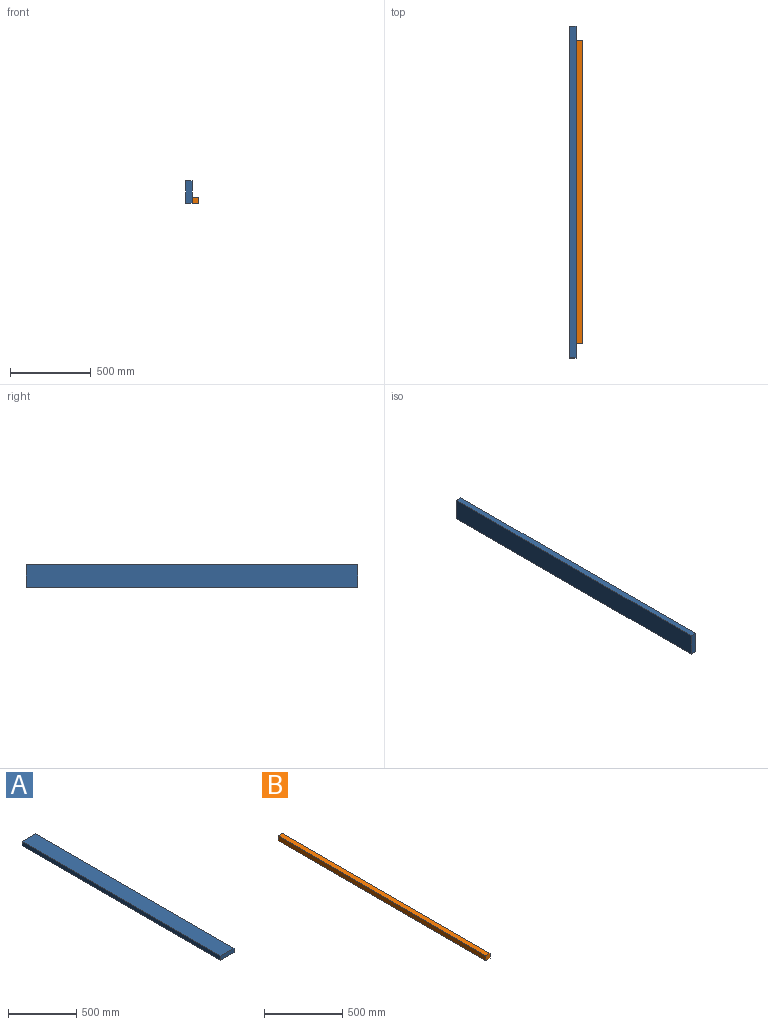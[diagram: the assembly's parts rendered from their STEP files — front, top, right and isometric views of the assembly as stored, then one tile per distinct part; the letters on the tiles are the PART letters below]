
ASSEMBLY  parts=2 mates=1
PART A: 6 faces, bbox 139.7x2057.4x38.1 mm
  f0: plane 2057.4x139.7mm, normal (0,0,1), area 287418.8mm2, adj f1,f3,f4,f5
  f1: plane 2057.4x38.1mm, normal (-1,0,0), area 78386.9mm2, adj f0,f2,f4,f5
  f2: plane 2057.4x139.7mm, normal (0,0,-1), area 287418.8mm2, adj f1,f3,f4,f5
  f3: plane 2057.4x38.1mm, normal (1,0,0), area 78386.9mm2, adj f0,f2,f4,f5
  f4: plane 139.7x38.1mm, normal (0,-1,0), area 5322.6mm2, adj f0,f1,f2,f3
  f5: plane 139.7x38.1mm, normal (0,1,0), area 5322.6mm2, adj f0,f1,f2,f3
PART B: 6 faces, bbox 38.1x1879.6x38.1 mm
  f0: plane 1879.6x38.1mm, normal (0,0,1), area 71612.8mm2, adj f1,f3,f4,f5
  f1: plane 1879.6x38.1mm, normal (-1,0,0), area 71612.8mm2, adj f0,f2,f4,f5
  f2: plane 1879.6x38.1mm, normal (0,0,-1), area 71612.8mm2, adj f1,f3,f4,f5
  f3: plane 1879.6x38.1mm, normal (1,0,0), area 71612.8mm2, adj f0,f2,f4,f5
  f4: plane 38.1x38.1mm, normal (0,1,0), area 1451.6mm2, adj f0,f1,f2,f3
  f5: plane 38.1x38.1mm, normal (0,-1,0), area 1451.6mm2, adj f0,f1,f2,f3
PLACE A rot(axis=(0,-1,0),90deg) t=(0,0,247.65)mm
PLACE B t=(38.1,88.9,19.05)mm
MATE fastened A.f2 <-> B.f1  axis (1,0,0) through (19.05,1028.7,0)mm
